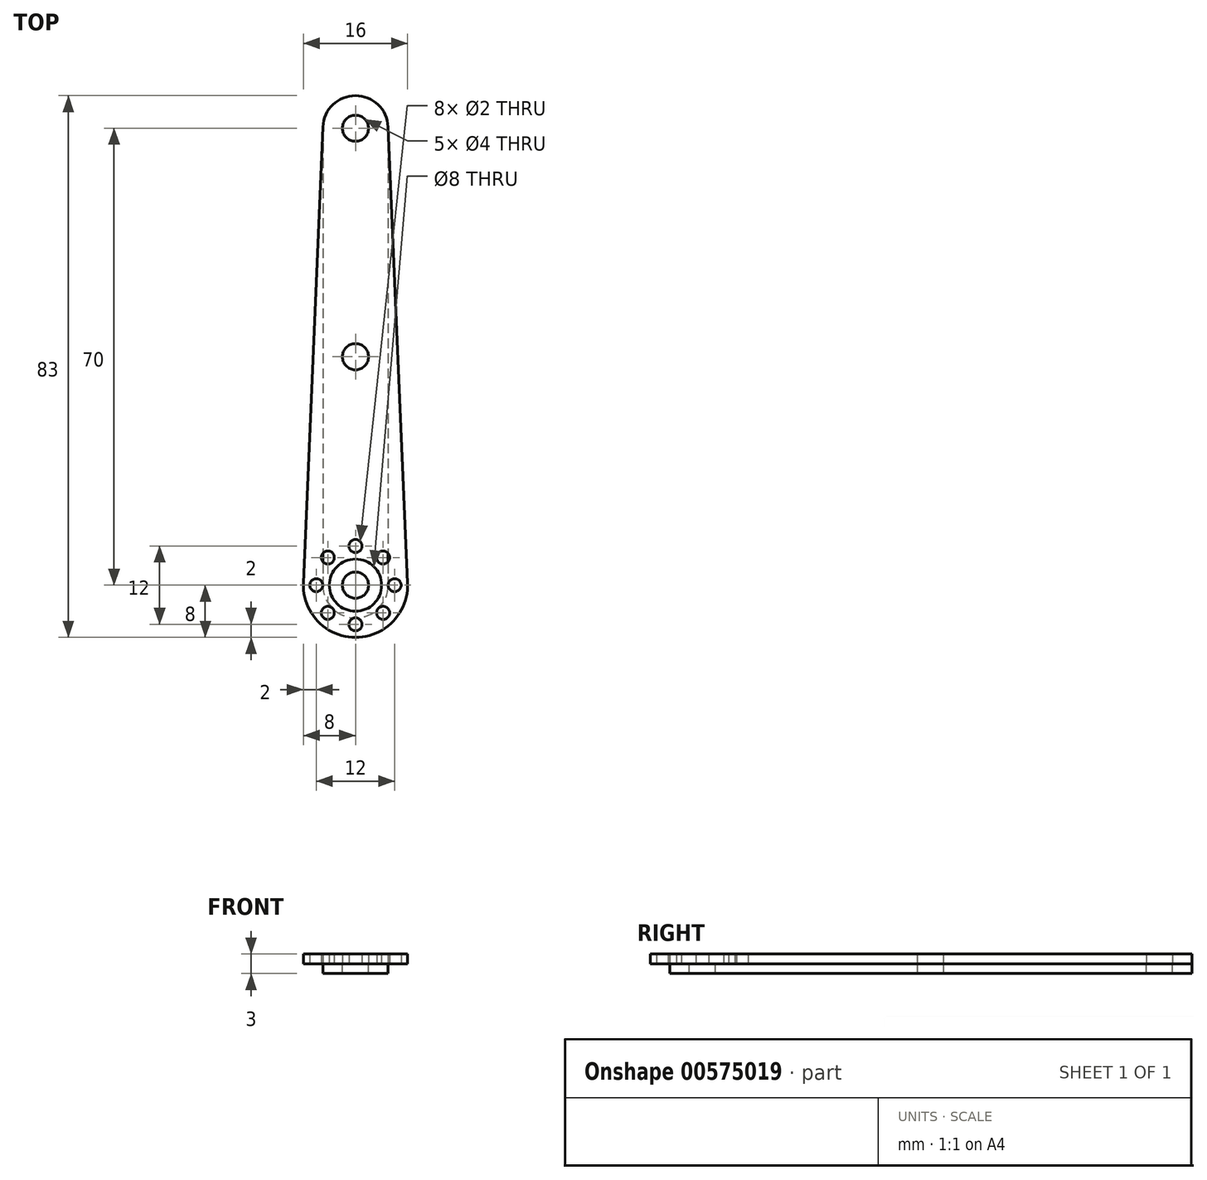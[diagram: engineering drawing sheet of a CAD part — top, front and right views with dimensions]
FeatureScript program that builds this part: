
annotation { "Feature Type Name" : "Feature", "Feature Type Description" : "" }
export const myFeature = defineFeature(function(context is Context, id is Id, definition is map)
    precondition{}
    {
        {
            var Q0;
            Q0=qCreatedBy(makeId("Top.planeOp"),FACE);
            var sketch = newSketch(context, id + "F0", { "sketchPlane" : qUnion([Q0])});
            skArc(sketch, "E0", {"start": v(-8, 0.34) * mm, "mid": v(0, -8) * mm, "end": v(8, 0.34) * mm});
            skCircle(sketch, "E1", {"center": v(0, 0) * mm, "radius": 4 * mm});
            skCircle(sketch, "E2", {"center": v(6, 0) * mm, "radius": 1 * mm});
            skCircle(sketch, "E3.1.0", {"center": v(4.24, 4.24) * mm, "radius": 1 * mm});
            skCircle(sketch, "E3.2.0", {"center": v(0, 6) * mm, "radius": 1 * mm});
            skCircle(sketch, "E3.3.0", {"center": v(-4.24, 4.24) * mm, "radius": 1 * mm});
            skCircle(sketch, "E3.4.0", {"center": v(-6, 0) * mm, "radius": 1 * mm});
            skCircle(sketch, "E3.5.0", {"center": v(-4.24, -4.24) * mm, "radius": 1 * mm});
            skCircle(sketch, "E3.6.0", {"center": v(0, -6) * mm, "radius": 1 * mm});
            skCircle(sketch, "E3.7.0", {"center": v(4.24, -4.24) * mm, "radius": 1 * mm});
            skCircle(sketch, "E4", {"center": v(0, 70) * mm, "radius": 2 * mm});
            skArc(sketch, "E5", {"start": v(5, 70.21) * mm, "mid": v(0, 75) * mm, "end": v(-5, 70.21) * mm});
            skLineSegment(sketch, "E6", {"start": v(-5, 70.21) * mm, "end": v(-8, 0.34) * mm});
            skLineSegment(sketch, "E7.MirrorCS", {"start": v(5, 70.21) * mm, "end": v(8, 0.34) * mm});
            skSolve(sketch);
        }
        {
            var Q0;
            Q0 = qSketchRegion(id + "F0", true);
            extrude(context, id + "F1", {"entities" : qUnion([Q0]), "depth" : 1.5 * mm, "offsetDistance" : 25 * mm});
        }
        {
            var Q0;
            Q0=qCreatedBy(makeId("Top.planeOp"),FACE);
            var sketch = newSketch(context, id + "F2", { "sketchPlane" : qUnion([Q0])});
            skCircle(sketch, "E8.0", {"center": v(0, 70) * mm, "radius": 2 * mm});
            skArc(sketch, "E9", {"start": v(5, 70) * mm, "mid": v(0, 75) * mm, "end": v(-5, 70) * mm});
            skLineSegment(sketch, "E10", {"start": v(0, 70) * mm, "end": v(0, 0) * mm, "construction": true});
            skLineSegment(sketch, "E11", {"start": v(0, 35) * mm, "end": v(-5, 35) * mm, "construction": true});
            skPoint(sketch, "E12", {"position": v(-5, 70) * mm});
            skPoint(sketch, "E13.MirrorP", {"position": v(5, 70) * mm});
            skLineSegment(sketch, "E14", {"start": v(-5, 70) * mm, "end": v(-5, 35) * mm});
            skLineSegment(sketch, "E15.MirrorCS", {"start": v(5, 70) * mm, "end": v(5, 35) * mm});
            skLineSegment(sketch, "E16.MirrorCS", {"start": v(-5, 0) * mm, "end": v(-5, 35) * mm});
            skCircle(sketch, "E17.MirrorC", {"center": v(0, 0) * mm, "radius": 2 * mm});
            skArc(sketch, "E18.MirrorCS", {"start": v(5, 0) * mm, "mid": v(0, -5) * mm, "end": v(-5, 0) * mm});
            skLineSegment(sketch, "E19.MirrorCS", {"start": v(5, 0) * mm, "end": v(5, 35) * mm});
            skSolve(sketch);
        }
        {
            var Q0;
            Q0 = qSketchRegion(id + "F2", true);
            extrude(context, id + "F3", {"entities" : qUnion([Q0]), "oppositeDirection" : true, "depth" : 1.5 * mm, "offsetDistance" : 25 * mm});
        }
        {
            var Q0;
            Q0=makeQuery(id+"F1.opExtrude","CAP_FACE",FACE,{"disambiguationData":[OSD([sQuery(id+"F0.wireOp",EDGE,"E0"),sQuery(id+"F0.wireOp",EDGE,"E1"),sQuery(id+"F0.wireOp",EDGE,"E2"),sQuery(id+"F0.wireOp",EDGE,"E3.1.0"),sQuery(id+"F0.wireOp",EDGE,"E3.2.0"),sQuery(id+"F0.wireOp",EDGE,"E3.3.0"),sQuery(id+"F0.wireOp",EDGE,"E3.4.0"),sQuery(id+"F0.wireOp",EDGE,"E3.5.0"),sQuery(id+"F0.wireOp",EDGE,"E3.6.0"),sQuery(id+"F0.wireOp",EDGE,"E3.7.0"),sQuery(id+"F0.wireOp",EDGE,"E4"),sQuery(id+"F0.wireOp",EDGE,"E5"),sQuery(id+"F0.wireOp",EDGE,"E6"),sQuery(id+"F0.wireOp",EDGE,"E7.MirrorCS")])],"isStart":false});
            var sketch = newSketch(context, id + "F4", { "sketchPlane" : qUnion([Q0])});
            skLineSegment(sketch, "E20", {"start": v(0, 70) * mm, "end": v(0, 0) * mm, "construction": true});
            skCircle(sketch, "E21", {"center": v(0, 35) * mm, "radius": 2 * mm});
            skSolve(sketch);
        }
        {
            var Q0;
            Q0 = qSketchRegion(id + "F4", true);
            extrude(context, id + "F5", {"entities" : qUnion([Q0]), "operationType" : NewBodyOperationType.REMOVE, "endBound" : BoundingType.THROUGH_ALL, "oppositeDirection" : true, "depth" : 25 * mm, "offsetDistance" : 25 * mm});
        }
    });
